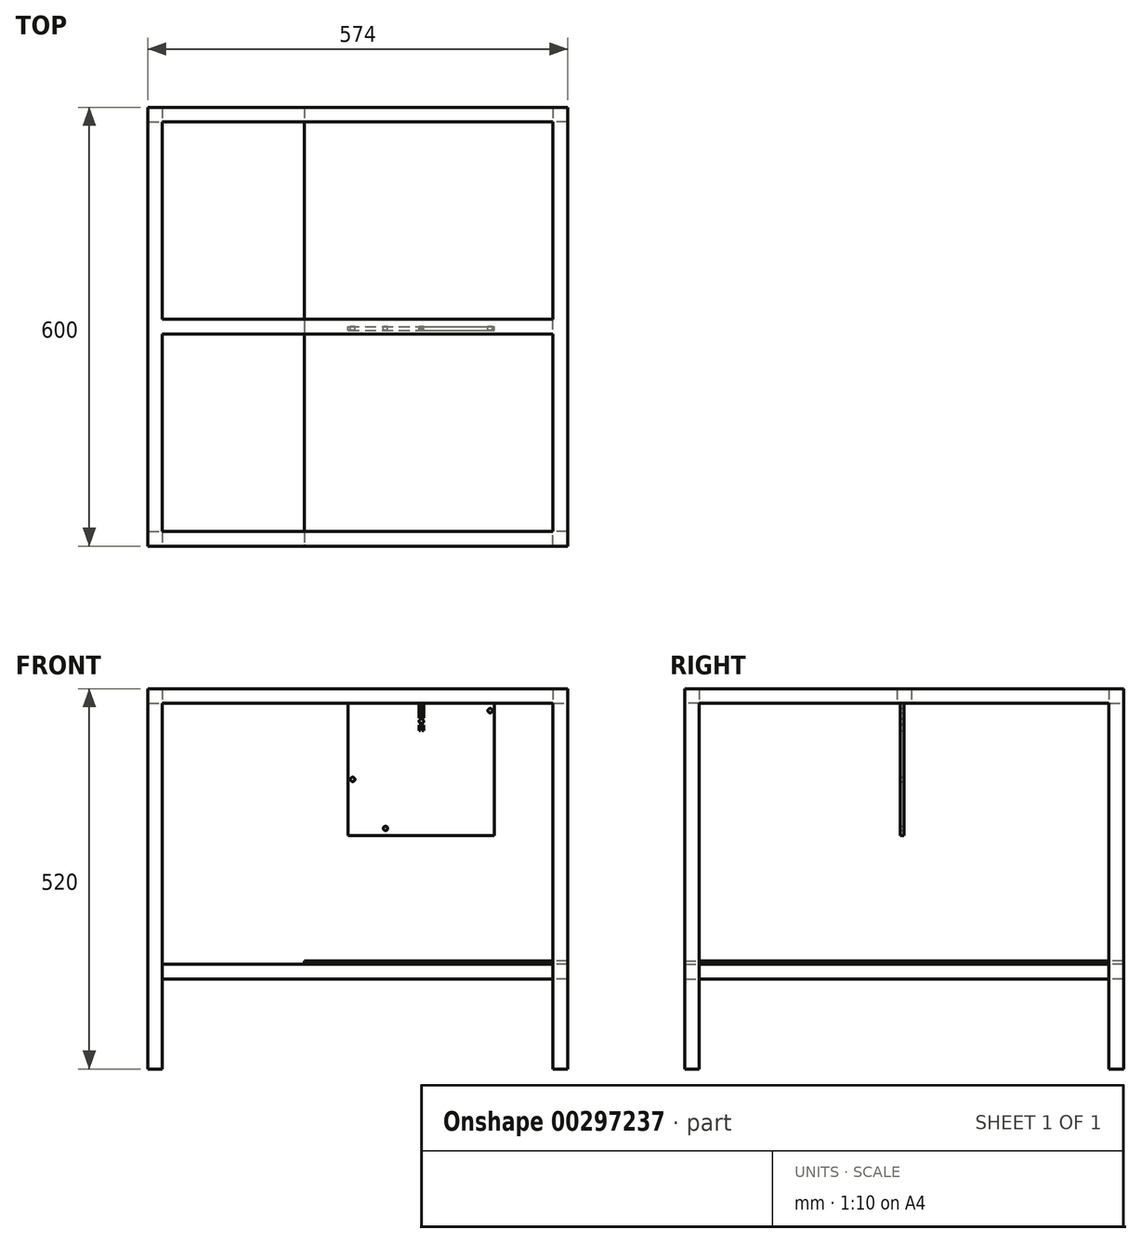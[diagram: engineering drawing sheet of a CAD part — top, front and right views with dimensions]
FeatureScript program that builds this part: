
annotation { "Feature Type Name" : "Feature", "Feature Type Description" : "" }
export const myFeature = defineFeature(function(context is Context, id is Id, definition is map)
    precondition{}
    {
        {
            var Q0;
            Q0=qCreatedBy(makeId("Front.planeOp"),FACE);
            var sketch = newSketch(context, id + "F0", { "sketchPlane" : qUnion([Q0])});
            skCircle(sketch, "E0", {"center": v(0, 0) * mm, "radius": 3 * mm});
            skCircle(sketch, "E1", {"center": v(-45, 67) * mm, "radius": 3 * mm});
            skCircle(sketch, "E2", {"center": v(143, 161) * mm, "radius": 3 * mm});
            skLineSegment(sketch, "E3.bottom", {"start": v(-51, -10) * mm, "end": v(149, -10) * mm});
            skLineSegment(sketch, "E3.top", {"start": v(-51, 171) * mm, "end": v(45.95, 171) * mm});
            skLineSegment(sketch, "E3.left", {"start": v(-51, -10) * mm, "end": v(-51, 171) * mm});
            skLineSegment(sketch, "E3.right", {"start": v(149, -10) * mm, "end": v(149, 171) * mm});
            skCircle(sketch, "E4", {"center": v(49, 146.5) * mm, "radius": 3 * mm});
            skPoint(sketch, "E4.centerSnap0", {"position": v(49, 171) * mm});
            skLineSegment(sketch, "E5.top", {"start": v(45.95, 151) * mm, "end": v(48.05, 151) * mm});
            skLineSegment(sketch, "E5.left", {"start": v(45.95, 171) * mm, "end": v(45.95, 151) * mm});
            skLineSegment(sketch, "E5.right", {"start": v(48.05, 171) * mm, "end": v(48.05, 151) * mm});
            skLineSegment(sketch, "E6.bottom", {"start": v(45.95, 141.5) * mm, "end": v(48.05, 141.5) * mm});
            skLineSegment(sketch, "E6.top", {"start": v(45.95, 133.5) * mm, "end": v(48.05, 133.5) * mm});
            skLineSegment(sketch, "E6.left", {"start": v(45.95, 141.5) * mm, "end": v(45.95, 133.5) * mm});
            skLineSegment(sketch, "E6.right", {"start": v(48.05, 141.5) * mm, "end": v(48.05, 133.5) * mm});
            skLineSegment(sketch, "E7.trimOffspring", {"start": v(48.05, 171) * mm, "end": v(149, 171) * mm});
            skLineSegment(sketch, "E8.MirrorCS", {"start": v(52.05, 133.5) * mm, "end": v(49.95, 133.5) * mm});
            skLineSegment(sketch, "E9.MirrorCS", {"start": v(52.05, 141.5) * mm, "end": v(49.95, 141.5) * mm});
            skLineSegment(sketch, "E10.MirrorCS", {"start": v(49.95, 171) * mm, "end": v(49.95, 151) * mm});
            skLineSegment(sketch, "E11.MirrorCS", {"start": v(52.05, 151) * mm, "end": v(49.95, 151) * mm});
            skLineSegment(sketch, "E12.MirrorCS", {"start": v(52.05, 141.5) * mm, "end": v(52.05, 133.5) * mm});
            skLineSegment(sketch, "E13.MirrorCS", {"start": v(49.95, 141.5) * mm, "end": v(49.95, 133.5) * mm});
            skLineSegment(sketch, "E14.MirrorCS", {"start": v(52.05, 171) * mm, "end": v(52.05, 151) * mm});
            skSolve(sketch);
        }
        {
            var Q0;
            Q0=makeQuery(id+"F0.imprint","IMPRINT",FACE,{"disambiguationData":[TD([[makeQuery(id+"F0.imprint","IMPRINT",EDGE,{"derivedFrom":sQuery(id+"F0.wireOp",EDGE,"E0")}),-1.0]])]});
            extrude(context, id + "F1", {"entities" : qUnion([Q0]), "depth" : 5 * mm});
        }
        {
            var Q0;
            Q0=qCreatedBy(makeId("Top.planeOp"),FACE);
            cPlane(context, id + "F2", {"entities" : qUnion([Q0]), "cplaneType" : CPlaneType.OFFSET, "offset" : 171 * mm, "width" : 150 * mm, "height" : 150 * mm});
        }
        {
            var Q0;
            Q0=qCreatedBy(id+"F2.planeOp",FACE);
            var sketch = newSketch(context, id + "F3", { "sketchPlane" : qUnion([Q0])});
            skLineSegment(sketch, "E15.bottom", {"start": v(249, -300) * mm, "end": v(229, -300) * mm});
            skLineSegment(sketch, "E15.top", {"start": v(249, 300) * mm, "end": v(229, 300) * mm});
            skLineSegment(sketch, "E15.left", {"start": v(249, -300) * mm, "end": v(249, 300) * mm});
            skLineSegment(sketch, "E15.right", {"start": v(229, -280) * mm, "end": v(229, 280) * mm});
            skLineSegment(sketch, "E16.bottom", {"start": v(229, 300) * mm, "end": v(-305, 300) * mm});
            skLineSegment(sketch, "E16.top", {"start": v(229, 280) * mm, "end": v(-305, 280) * mm});
            skLineSegment(sketch, "E17.bottom", {"start": v(229, -300) * mm, "end": v(-305, -300) * mm});
            skLineSegment(sketch, "E17.top", {"start": v(229, -280) * mm, "end": v(-305, -280) * mm});
            skLineSegment(sketch, "E18.bottom", {"start": v(-305, 300) * mm, "end": v(-325, 300) * mm});
            skLineSegment(sketch, "E18.top", {"start": v(-305, -300) * mm, "end": v(-325, -300) * mm});
            skLineSegment(sketch, "E18.left", {"start": v(-305, 280) * mm, "end": v(-305, -280) * mm});
            skLineSegment(sketch, "E18.right", {"start": v(-325, 300) * mm, "end": v(-325, -300) * mm});
            skPoint(sketch, "E19", {"position": v(249, 0) * mm});
            skLineSegment(sketch, "E20.bottom", {"start": v(229, -10) * mm, "end": v(-305, -10) * mm});
            skLineSegment(sketch, "E20.top", {"start": v(229, 10) * mm, "end": v(-305, 10) * mm});
            skLineSegment(sketch, "E20.left", {"start": v(229, -10) * mm, "end": v(229, 10) * mm});
            skLineSegment(sketch, "E20.right", {"start": v(-305, -10) * mm, "end": v(-305, 10) * mm});
            skPoint(sketch, "E20.middle", {"position": v(-38, 0) * mm});
            skSolve(sketch);
        }
        {
            var Q0;
            Q0=qSketchRegion(id+"F3",true);
            var Q1;
            Q1=makeQuery(id+"F3.imprint","IMPRINT",FACE,{"disambiguationData":[TD([[makeQuery(id+"F3.imprint","IMPRINT",EDGE,{"derivedFrom":sQuery(id+"F3.wireOp",EDGE,"E20.bottom")}),-1.0]])]});
            extrude(context, id + "F4", {"entities" : qUnion([Q0, Q1]), "operationType" : NewBodyOperationType.ADD, "depth" : 20 * mm});
        }
        {
            var Q0;
            Q0=makeQuery(id+"F4.opExtrude","CAP_FACE",FACE,{"disambiguationData":[OSD([sQuery(id+"F3.wireOp",EDGE,"E15.bottom"),sQuery(id+"F3.wireOp",EDGE,"E15.top"),sQuery(id+"F3.wireOp",EDGE,"E15.left"),sQuery(id+"F3.wireOp",EDGE,"E15.right"),sQuery(id+"F3.wireOp",EDGE,"7mnNWSTb-ftgJ-FYnv-rSfW-03W7qfMdHJeY.bottom"),sQuery(id+"F3.wireOp",EDGE,"7mnNWSTb-ftgJ-FYnv-rSfW-03W7qfMdHJeY.top"),sQuery(id+"F3.wireOp",EDGE,"yphk7Mg7-LXwZ-R6qe-Yzbn-fpSbBpRDTs4J.bottom"),sQuery(id+"F3.wireOp",EDGE,"yphk7Mg7-LXwZ-R6qe-Yzbn-fpSbBpRDTs4J.top"),sQuery(id+"F3.wireOp",EDGE,"yphk7Mg7-LXwZ-R6qe-Yzbn-fpSbBpRDTs4J.left"),sQuery(id+"F3.wireOp",EDGE,"yphk7Mg7-LXwZ-R6qe-Yzbn-fpSbBpRDTs4J.right"),sQuery(id+"F3.wireOp",EDGE,"9GNo11h2-buUj-PFzF-0UOW-2sDmyF7RkODV.bottom"),sQuery(id+"F3.wireOp",EDGE,"9GNo11h2-buUj-PFzF-0UOW-2sDmyF7RkODV.top")])],"isStart":true});
            var sketch = newSketch(context, id + "F5", { "sketchPlane" : qUnion([Q0])});
            skLineSegment(sketch, "E21.bottom", {"start": v(-325, 300) * mm, "end": v(-305, 300) * mm});
            skLineSegment(sketch, "E21.top", {"start": v(-325, 280) * mm, "end": v(-305, 280) * mm});
            skLineSegment(sketch, "E21.left", {"start": v(-325, 300) * mm, "end": v(-325, 280) * mm});
            skLineSegment(sketch, "E21.right", {"start": v(-305, 300) * mm, "end": v(-305, 280) * mm});
            skLineSegment(sketch, "E22.bottom", {"start": v(-325, -300) * mm, "end": v(-305, -300) * mm});
            skLineSegment(sketch, "E22.top", {"start": v(-325, -280) * mm, "end": v(-305, -280) * mm});
            skLineSegment(sketch, "E22.left", {"start": v(-325, -300) * mm, "end": v(-325, -280) * mm});
            skLineSegment(sketch, "E22.right", {"start": v(-305, -300) * mm, "end": v(-305, -280) * mm});
            skLineSegment(sketch, "E23.bottom", {"start": v(229, -280) * mm, "end": v(249, -280) * mm});
            skLineSegment(sketch, "E23.top", {"start": v(229, -300) * mm, "end": v(249, -300) * mm});
            skLineSegment(sketch, "E23.left", {"start": v(229, -280) * mm, "end": v(229, -300) * mm});
            skLineSegment(sketch, "E23.right", {"start": v(249, -280) * mm, "end": v(249, -300) * mm});
            skLineSegment(sketch, "E24.bottom", {"start": v(229, 280) * mm, "end": v(249, 280) * mm});
            skLineSegment(sketch, "E24.top", {"start": v(229, 300) * mm, "end": v(249, 300) * mm});
            skLineSegment(sketch, "E24.left", {"start": v(229, 280) * mm, "end": v(229, 300) * mm});
            skLineSegment(sketch, "E24.right", {"start": v(249, 280) * mm, "end": v(249, 300) * mm});
            skSolve(sketch);
        }
        {
            var Q0;
            Q0=qSketchRegion(id+"F5",true);
            extrude(context, id + "F6", {"entities" : qUnion([Q0]), "operationType" : NewBodyOperationType.ADD, "depth" : 500 * mm});
        }
        {
            var Q0;
            Q0=qCreatedBy(makeId("Top.planeOp"),FACE);
            cPlane(context, id + "F7", {"entities" : qUnion([Q0]), "cplaneType" : CPlaneType.OFFSET, "offset" : 186 * mm, "oppositeDirection" : true, "width" : 150 * mm, "height" : 150 * mm});
        }
        {
            var Q0;
            Q0=qCreatedBy(id+"F7.planeOp",FACE);
            var sketch = newSketch(context, id + "F8", { "sketchPlane" : qUnion([Q0])});
            skPoint(sketch, "E25.middle", {"position": v(69, 0) * mm});
            skLineSegment(sketch, "E26.top", {"start": v(229, 300) * mm, "end": v(-111, 300) * mm});
            skLineSegment(sketch, "E27.top", {"start": v(229, -300) * mm, "end": v(-111, -300) * mm});
            skLineSegment(sketch, "E28", {"start": v(-111, 300) * mm, "end": v(-111, -300) * mm});
            skLineSegment(sketch, "E29", {"start": v(249, 280) * mm, "end": v(249, -280) * mm});
            skPoint(sketch, "E30", {"position": v(249, 0) * mm});
            skLineSegment(sketch, "E31.top", {"start": v(249, 280) * mm, "end": v(229, 280) * mm});
            skLineSegment(sketch, "E31.right", {"start": v(229, 300) * mm, "end": v(229, 280) * mm});
            skPoint(sketch, "E31.left.start.orphan", {"position": v(249, 300) * mm});
            skLineSegment(sketch, "E32.top", {"start": v(249, -280) * mm, "end": v(229, -280) * mm});
            skLineSegment(sketch, "E32.right", {"start": v(229, -300) * mm, "end": v(229, -280) * mm});
            skPoint(sketch, "E32.left.start.orphan", {"position": v(249, -300) * mm});
            skSolve(sketch);
        }
        {
            var Q0;
            Q0=qSketchRegion(id+"F8",true);
            extrude(context, id + "F9", {"entities" : qUnion([Q0]), "depth" : 5 * mm});
        }
        {
            var Q0;
            Q0=makeQuery(id+"F9.opExtrude","CAP_FACE",FACE,{"disambiguationData":[OSD([sQuery(id+"F8.wireOp",EDGE,"E26.top"),sQuery(id+"F8.wireOp",EDGE,"E27.top"),sQuery(id+"F8.wireOp",EDGE,"E28"),sQuery(id+"F8.wireOp",EDGE,"E29"),sQuery(id+"F8.wireOp",EDGE,"E31.top"),sQuery(id+"F8.wireOp",EDGE,"E31.right"),sQuery(id+"F8.wireOp",EDGE,"E32.top"),sQuery(id+"F8.wireOp",EDGE,"E32.right")])],"isStart":true});
            var sketch = newSketch(context, id + "F10", { "sketchPlane" : qUnion([Q0])});
            skPoint(sketch, "E33.oppositeSnap0", {"position": v(239, 280) * mm});
            skLineSegment(sketch, "E34.bottom", {"start": v(229, 280) * mm, "end": v(249, 280) * mm});
            skLineSegment(sketch, "E34.top", {"start": v(229, -280) * mm, "end": v(249, -280) * mm});
            skLineSegment(sketch, "E34.left", {"start": v(229, 280) * mm, "end": v(229, -280) * mm});
            skLineSegment(sketch, "E34.right", {"start": v(249, 280) * mm, "end": v(249, -280) * mm});
            skLineSegment(sketch, "E35.bottom", {"start": v(229, 280) * mm, "end": v(-305, 280) * mm});
            skLineSegment(sketch, "E35.top", {"start": v(229, 300) * mm, "end": v(-305, 300) * mm});
            skLineSegment(sketch, "E35.left", {"start": v(229, 280) * mm, "end": v(229, 300) * mm});
            skLineSegment(sketch, "E35.right", {"start": v(-305, 280) * mm, "end": v(-305, 300) * mm});
            skLineSegment(sketch, "E36.bottom", {"start": v(229, -300) * mm, "end": v(-305, -300) * mm});
            skLineSegment(sketch, "E36.top", {"start": v(229, -280) * mm, "end": v(-305, -280) * mm});
            skLineSegment(sketch, "E36.left", {"start": v(229, -300) * mm, "end": v(229, -280) * mm});
            skLineSegment(sketch, "E36.right", {"start": v(-305, -300) * mm, "end": v(-305, -280) * mm});
            skSolve(sketch);
        }
        {
            var Q0;
            Q0=qSketchRegion(id+"F10",true);
            extrude(context, id + "F11", {"entities" : qUnion([Q0]), "depth" : 20 * mm});
        }
    });
